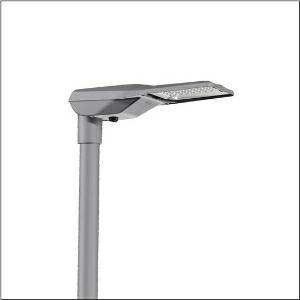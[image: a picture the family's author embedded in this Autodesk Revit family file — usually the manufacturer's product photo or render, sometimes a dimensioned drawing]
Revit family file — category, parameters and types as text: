
# Revit family: streetlight_sl_21_mini___p0_5a_5xe2v33r08jb_a833
name_source: partatom
category: Lighting Fixtures
units: mm (PartAtom-declared; Revit-internal decimal feet)

## family parameters
Cut with Voids When Loaded = No
Host = Face
Light Source = No
Part Type = Normal
Room Calculation Point = No
Round Connector Dimension = Use Diameter
Shared = No

## types (1)
- --- (1 x LED, 12720 lm, 88.6 W, 3000K)
    Apparent Load = 89 VA
    CIE Flux Codes = 37 73 96 100 100
    Color Rendering = 70
    Color Temperature = 3000K
    Default Elevation = 1800 mm
    Description = Streetlight SL 21 mini, mast luminaire, primary light control with lens, of PMMA, primary optical cover: cover, of toughened safety glass, transparent, light distribution: P0.5a, light emission: direct distribution, primary light characteristic: asymmetric, installation type: post-top, side-entry, LED, High Power LED, rated luminous flux: 12.720lm, luminous efficacy: 144lm/W, light colour: 730, colour temperature: 3000K, control gear: D4i, control: pre-setting: logarithmic dimming characteristic, flexible luminous flux parameterisation, time-dependent luminous flux control, constant luminous flux control, overheat protection, mains connection: 220..240V, AC, 50/60Hz, start of lifetime: 89W, end of service life: 92W, reduction: 41W, luminaire housing, of diecast aluminium, powder-coated, SITECO metallic grey (DB 702S), corrosivity category C5 high according to DIN EN ISO 12944, multi-level sealing system, sealing non-destructively replaceable, inclination adjustable: 0°, 5°, 10°, 15°, please order mast flange separately, length: 628mm, width: 235mm, height: 110mm, mast flange for spigot size: 42mm (side-entry): 5XC10008XM4, 60/48mm (side-entry/post-top): 5XC10108XM2, 76/60mm (side-entry/post-top): 5XC10108XM1, mounting height: 4..8m, Smart Interface below, protection rating (complete): IP66, insulation class (complete): insulation class II (safety insulation), certification: CE, ENEC, ENEC+, VDE, impact resistance: IK10, permissible operating ambient temperature for outdoor applications: -40..+50°C, standard-compliant lighting for roads and squares, packaging unit: 1 piece

Light Distribution: P0.5a
    Height = 110 mm
    Lamp = 1 x LED
    Lamp Light Flux = 12720 lm
    Lamp Power = 88.6 W
    Lamp count = 1
    Length = 625 mm
    Luminous efficacy = 144 lm/W
    Manufacturer = Siteco
    ModVariant = No
    Model = 5XE2V33R08JB
    Number of Poles = 1
    OnlyDefault = Yes
    Power Factor = 1
    Product Name = Streetlight SL 21 mini | P0.5a
    Product group = mast luminaire | pylon top
    ProductGroupID = 6100
    Protection Class = Protection class II
    Protection Degree = IP 66
    RLX_Detail_Level = 1
    RLX_Emergency_Light_Flux = 0 lm
    RLX_Emergency_Type = 0
    RLX_Emergency_Type_DB = No
    RlxData = <blob elided: 26053 chars, md5=fc673ad0>
    Socket = socket
    Standby Power = 0 W
    System Light Flux = 12720 lm
    System Power = 89 W
    Type Comments = factory setting: luminous flux: 100 % | dim-lin: 254 | 915 mA
    Type Image = l_1003516.jpg
    URL = http://relux.com
    VarID = @adj_032773
    Voltage = 0 V
    Weight = 0.00 kg
    Width = 234 mm

## geometry (parser evidence)
native form markers: Blend x4, Sweep x8
no freeform markers — native parametric forms only
